# Revit family: Legrand coffret photovoltaïque pré-équipé
name_source: partatom
category: Equipement électrique
revit_build: Autodesk Revit 2018 (Build: 20170223_1515(x64)
units: mm (PartAtom-declared; Revit-internal decimal feet)

## family parameters
Basée sur le plan de construction = Non
Configuration du panneau = Deux colonnes, circuits au sein
Cote de connecteur circulaire = Utiliser le diamètre
Couper avec des vides une fois chargée = Non
Numéro OmniClass = 23.80.30.11.17
Partagée = Non
Point de calcul de pièce = Non
Titre OmniClass = Distribution Boards and Control Panels
Toujours verticalement = Oui
Type d'élément = Tableau de raccordement

## types (3) — shared parameters
Conditions Générale d'Utilisation = https://export.legrand.com
ETIM Class 6.0 = EC000214
Fabricant = Legrand
IK = 09
IP = 65
Image du type = Plexo3_12_modules_001922_pw_153883_pz_0.jpg
Matière = Polystyrène
Polystyrène
RAL = 7046
URL = www.legrand.fr

## per-type parameters (varying)
| type | Coffret 414001 | Coffret 414003 | Coffret 414020 | Câble avec connecteur type MC4 (raccordement aval) | Interrupteur différentiel | Interrupteur sectionneur | Kit de signalétique photovoltaïque | Parafoudre protégé | Partie AC | Partie DC | connecteur type MC4 | disjoncteur |
| Legrand coffret pré-équipé 3kWc DC 414003 | Non | Oui | Non |  |  | 25A 600V | Oui |  | Non | Oui | raccordement |  |
| Legrand coffret pré-équipé 3kWc DC + AC 414001 | Oui | Non | Non | connecteur aval | 30 mA type F (ex Hpi) | 25A 600V | Oui | type 2 - 12kA (0 039 51) | Oui | Oui | raccordement | DNX³ 4.5kA 20A courbe C |
| Legrand coffret pré-équipé  AC 220V 414020 | Non | Non | Oui |  | 30 mA type F (ex Hpi) |  | Non | type 2 - 12kA (0 039 51) | Oui | Non |  | DNX³ 4.5kA 20A courbe C |

note: column(s) folded — value = type name in every type: Description
